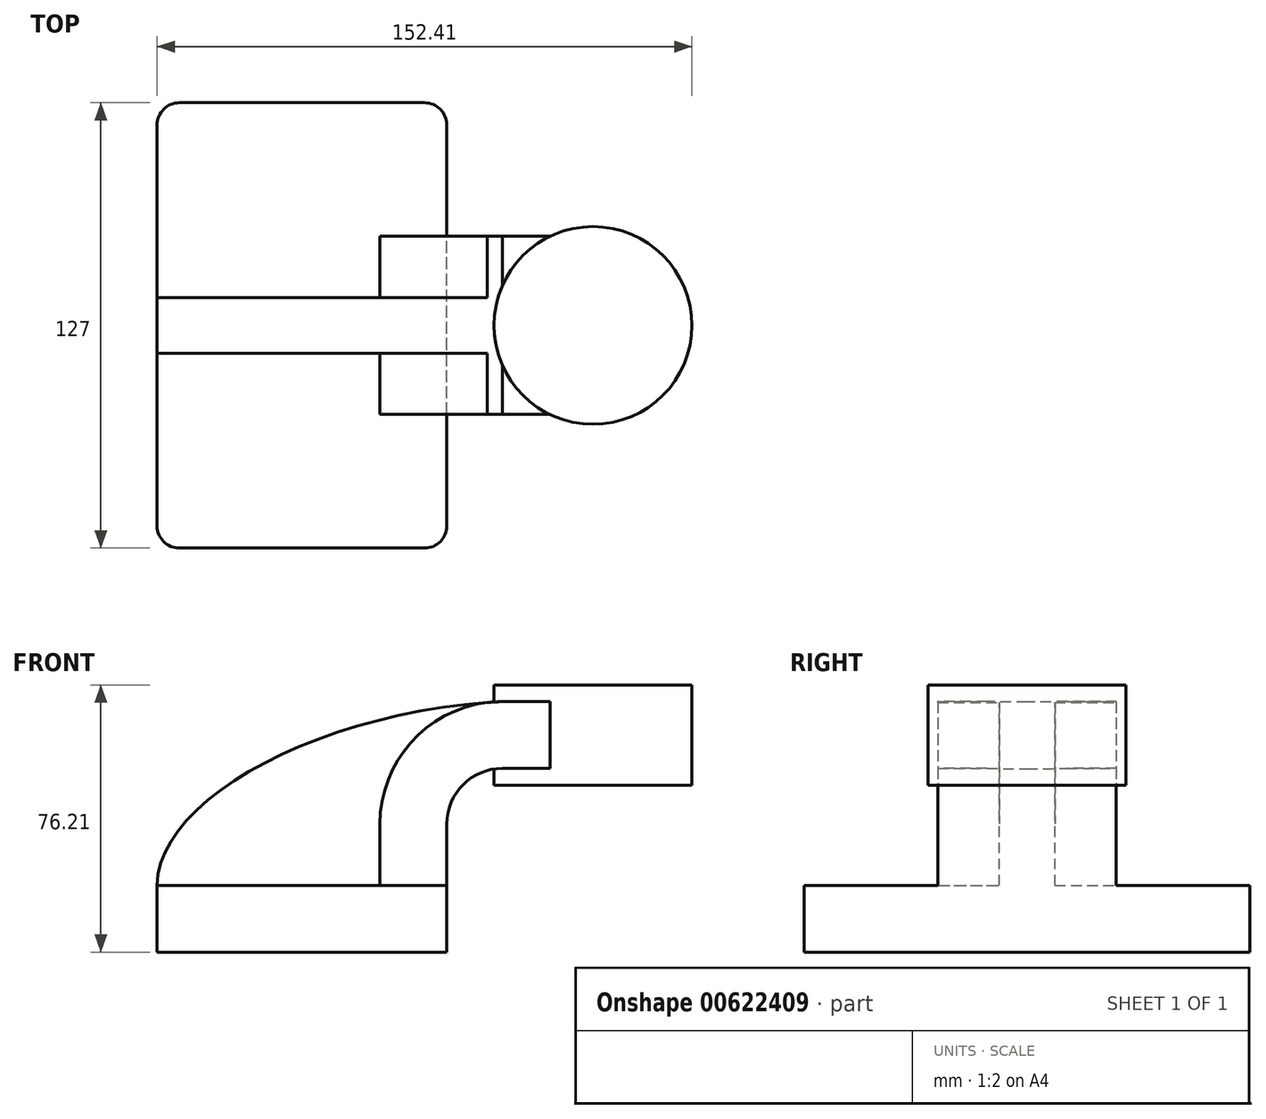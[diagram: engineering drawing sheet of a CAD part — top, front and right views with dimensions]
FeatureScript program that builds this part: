
annotation { "Feature Type Name" : "Feature", "Feature Type Description" : "" }
export const myFeature = defineFeature(function(context is Context, id is Id, definition is map)
    precondition{}
    {
        {
            var Q0;
            Q0=qCreatedBy(makeId("Front.planeOp"),FACE);
            var sketch = newSketch(context, id + "F0", { "sketchPlane" : qUnion([Q0])});
            skLineSegment(sketch, "E0.bottom", {"start": v(-41.28, -9.53) * mm, "end": v(41.28, -9.53) * mm});
            skLineSegment(sketch, "E0.top", {"start": v(-41.28, 9.53) * mm, "end": v(41.28, 9.53) * mm});
            skLineSegment(sketch, "E0.left", {"start": v(-41.28, -9.53) * mm, "end": v(-41.28, 9.53) * mm});
            skLineSegment(sketch, "E0.right", {"start": v(41.28, -9.53) * mm, "end": v(41.28, 9.53) * mm});
            skPoint(sketch, "E0.middle", {"position": v(0, 0) * mm});
            skLineSegment(sketch, "E1.bottom", {"start": v(60.33, 38.1) * mm, "end": v(111.12, 38.1) * mm});
            skLineSegment(sketch, "E1.top", {"start": v(60.33, 66.67) * mm, "end": v(111.12, 66.67) * mm});
            skLineSegment(sketch, "E1.left", {"start": v(60.33, 38.1) * mm, "end": v(60.33, 66.67) * mm});
            skLineSegment(sketch, "E1.right", {"start": v(111.12, 38.1) * mm, "end": v(111.12, 66.67) * mm});
            skPoint(sketch, "E1.middle", {"position": v(85.72, 52.39) * mm});
            skLineSegment(sketch, "E2", {"start": v(41.27, 9.53) * mm, "end": v(41.27, 27) * mm});
            skArc(sketch, "E3", {"start": v(41.27, 27) * mm, "mid": v(45.92, 38.23) * mm, "end": v(57.15, 42.88) * mm});
            skLineSegment(sketch, "E4", {"start": v(57.15, 42.88) * mm, "end": v(82.93, 42.88) * mm});
            skLineSegment(sketch, "E5.0", {"start": v(57.15, 61.93) * mm, "end": v(82.93, 61.93) * mm});
            skArc(sketch, "E5.1", {"start": v(22.23, 27) * mm, "mid": v(32.45, 51.7) * mm, "end": v(57.15, 61.93) * mm});
            skLineSegment(sketch, "E5.2", {"start": v(22.22, 9.53) * mm, "end": v(22.22, 27) * mm});
            skLineSegment(sketch, "E6", {"start": v(82.93, 38.1) * mm, "end": v(82.93, 66.67) * mm});
            skPoint(sketch, "E6.startSnap0", {"position": v(85.72, 38.1) * mm});
            skFitSpline(sketch, "E7", {"points": [v(-41.28, 9.53) * mm, v(57.15, 61.93) * mm], "startDerivative": vector(0.45, 74.02) * mm, "endDerivative": vector(154.92, 7.71) * mm});
            skSolve(sketch);
        }
        {
            var Q0;
            Q0=makeQuery(id+"F0.imprint","IMPRINT",FACE,{"disambiguationData":[TD([[makeQuery(id+"F0.imprint","IMPRINT",EDGE,{"derivedFrom":sQuery(id+"F0.wireOp",EDGE,"E0.bottom")}),1.0]])]});
            extrude(context, id + "F1", {"entities" : qUnion([Q0]), "endBound" : BoundingType.SYMMETRIC, "depth" : 127 * mm, "offsetDistance" : 25.4 * mm});
        }
        {
            var Q0;
            {var subQ1=sQuery(id+"F0.wireOp",EDGE,"E2");Q0=makeQuery(id+"F0.imprint","IMPRINT",FACE,{"disambiguationData":[TD([[makeQuery(id+"F0.imprint","IMPRINT",EDGE,{"derivedFrom":subQ1}),1.0]])]});}
            var Q1;
            {var subQ0=sQuery(id+"F0.wireOp",EDGE,"E4");var subQ1=sQuery(id+"F0.wireOp",EDGE,"E1.left");var subQ2=makeQuery(id+"F0.imprint","INTERSECT",VERTEX,{"derivedFrom":[subQ1,subQ0]});Q1=makeQuery(id+"F0.imprint","IMPRINT",FACE,{"disambiguationData":[TD([[makeQuery(id+"F0.imprint","IMPRINT",EDGE,{"disambiguationData":[TD([[subQ2,-1.0]])],"derivedFrom":subQ1}),-1.0]])]});}
            extrude(context, id + "F2", {"entities" : qUnion([Q0, Q1]), "operationType" : NewBodyOperationType.ADD, "endBound" : BoundingType.SYMMETRIC, "depth" : 50.8 * mm, "offsetDistance" : 25.4 * mm});
        }
        {
            var Q0;
            {var subQ3=sQuery(id+"F0.wireOp",EDGE,"E5.2");Q0=makeQuery(id+"F0.imprint","IMPRINT",FACE,{"disambiguationData":[TD([[makeQuery(id+"F0.imprint","IMPRINT",EDGE,{"derivedFrom":subQ3}),1.0]])]});}
            extrude(context, id + "F3", {"entities" : qUnion([Q0]), "operationType" : NewBodyOperationType.ADD, "endBound" : BoundingType.SYMMETRIC, "depth" : 15.88 * mm, "offsetDistance" : 25.4 * mm});
        }
        {
            var Q0;
            {var subQ4=sQuery(id+"F0.wireOp",EDGE,"E1.right");Q0=makeQuery(id+"F0.imprint","IMPRINT",FACE,{"disambiguationData":[TD([[makeQuery(id+"F0.imprint","IMPRINT",EDGE,{"derivedFrom":subQ4}),1.0]])]});}
            var Q1;
            Q1=sQuery(id+"F0.wireOp",EDGE,"E6");
            revolve(context, id + "F4", {"operationType" : NewBodyOperationType.ADD, "entities" : qUnion([Q0]), "axis" : qUnion([Q1]), "revolveType" : RevolveType.FULL});
        }
        {
            var Q0;
            Q0=makeQuery(id+"F1.opExtrude","CAP_EDGE",EDGE,{"disambiguationData":[OSD([sQuery(id+"F0.wireOp",EDGE,"E0.left")])],"isStart":false});
            var Q1;
            Q1=makeQuery(id+"F1.opExtrude","CAP_EDGE",EDGE,{"disambiguationData":[OSD([sQuery(id+"F0.wireOp",EDGE,"E0.right")])],"isStart":false});
            var Q2;
            Q2=makeQuery(id+"F1.opExtrude","CAP_EDGE",EDGE,{"disambiguationData":[OSD([sQuery(id+"F0.wireOp",EDGE,"E0.right")])],"isStart":true});
            var Q3;
            Q3=makeQuery(id+"F1.opExtrude","CAP_EDGE",EDGE,{"disambiguationData":[OSD([sQuery(id+"F0.wireOp",EDGE,"E0.left")])],"isStart":true});
            fillet(context, id + "F5", {"entities" : qUnion([Q0, Q1, Q2, Q3]), "radius" : 6.35 * mm, "tangentPropagation" : true, "allowEdgeOverflow" : false});
        }
    });
